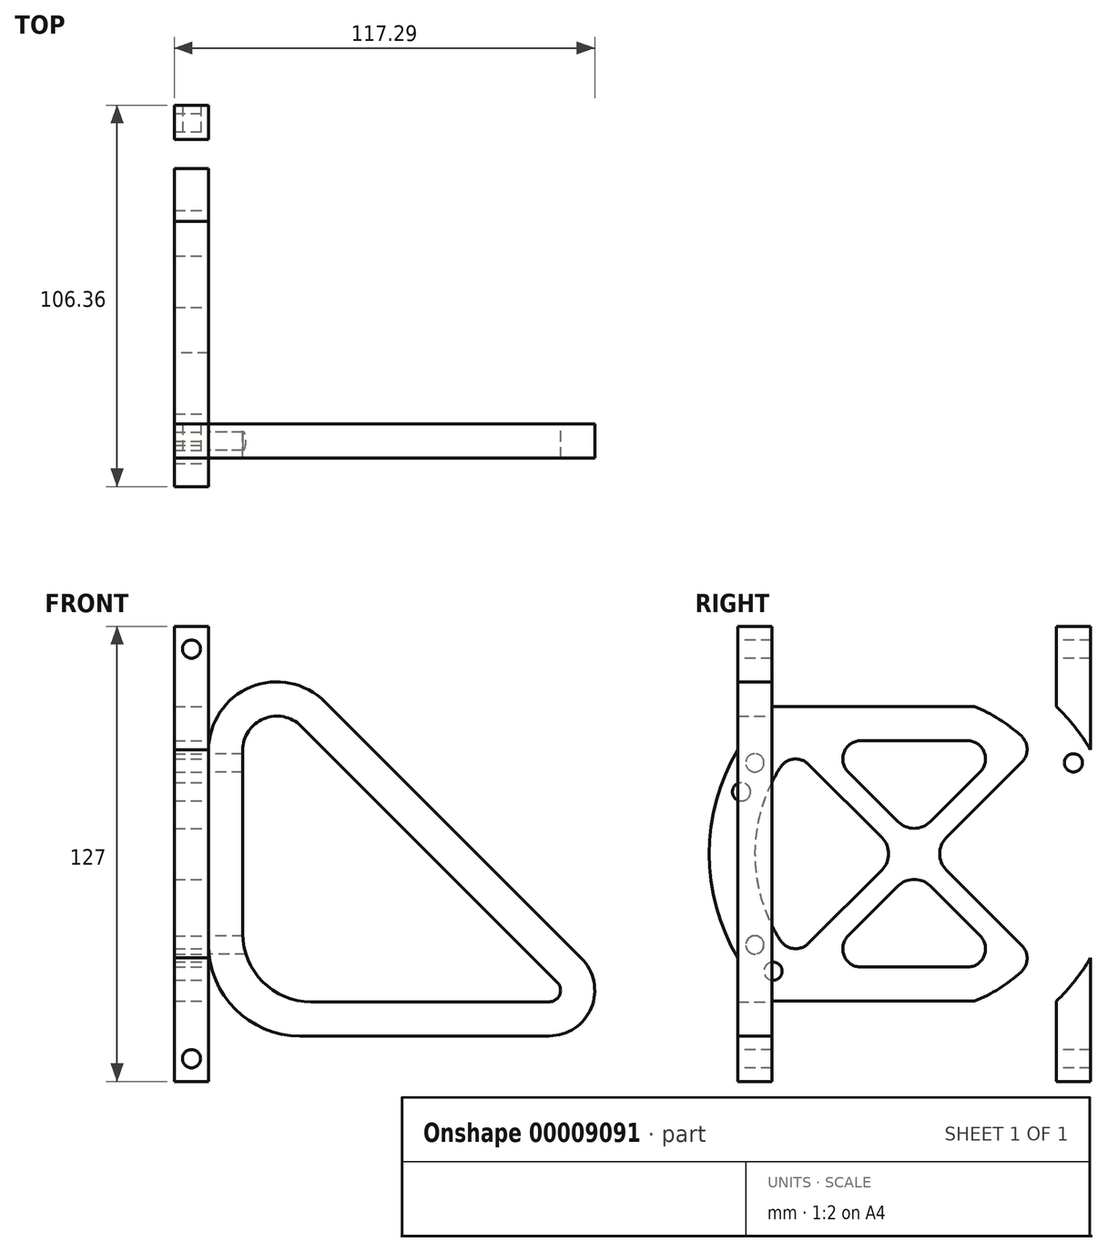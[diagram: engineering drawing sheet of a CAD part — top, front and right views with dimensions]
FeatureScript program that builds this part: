
annotation { "Feature Type Name" : "Feature", "Feature Type Description" : "" }
export const myFeature = defineFeature(function(context is Context, id is Id, definition is map)
    precondition{}
    {
        {
            var Q0;
            Q0=qCreatedBy(makeId("Front.planeOp"),FACE);
            var sketch = newSketch(context, id + "F6", { "sketchPlane" : qUnion([Q0])});
            skLineSegment(sketch, "E0", {"start": v(32.52, -32.52) * mm, "end": v(104.04, -104.04) * mm});
            skLineSegment(sketch, "E1", {"start": v(95.06, -125.72) * mm, "end": v(25.4, -125.72) * mm});
            skLineSegment(sketch, "E2", {"start": v(0, -46) * mm, "end": v(0, -100.32) * mm});
            skLineSegment(sketch, "E3.0", {"start": v(25.79, -39.26) * mm, "end": v(97.3, -110.78) * mm});
            skLineSegment(sketch, "E3.1", {"start": v(9.53, -46) * mm, "end": v(9.53, -97.15) * mm});
            skLineSegment(sketch, "E3.2", {"start": v(95.06, -116.2) * mm, "end": v(28.58, -116.2) * mm});
            skPoint(sketch, "E4.visualSharp", {"position": v(102.73, -116.2) * mm});
            skArc(sketch, "E4.filletArc", {"start": v(95.06, -116.2) * mm, "mid": v(98, -114.24) * mm, "end": v(97.3, -110.78) * mm});
            skPoint(sketch, "E5.visualSharp", {"position": v(9.53, -23) * mm});
            skArc(sketch, "E5.filletArc", {"start": v(25.79, -39.26) * mm, "mid": v(15.4, -37.2) * mm, "end": v(9.53, -46) * mm});
            skPoint(sketch, "E6.visualSharp", {"position": v(9.53, -116.2) * mm});
            skArc(sketch, "E6.filletArc", {"start": v(9.53, -97.15) * mm, "mid": v(15.1, -110.62) * mm, "end": v(28.58, -116.2) * mm});
            skPoint(sketch, "E7.visualSharp", {"position": v(0, -125.72) * mm});
            skArc(sketch, "E7.filletArc", {"start": v(0, -100.32) * mm, "mid": v(7.44, -118.28) * mm, "end": v(25.4, -125.72) * mm});
            skPoint(sketch, "E8.visualSharp", {"position": v(0, 0) * mm});
            skArc(sketch, "E8.filletArc", {"start": v(32.52, -32.52) * mm, "mid": v(11.76, -28.4) * mm, "end": v(0, -46) * mm});
            skPoint(sketch, "E9.visualSharp", {"position": v(125.72, -125.72) * mm});
            skArc(sketch, "E9.filletArc", {"start": v(95.06, -125.72) * mm, "mid": v(106.8, -117.88) * mm, "end": v(104.04, -104.04) * mm});
            skSolve(sketch);
        }
        {
            var Q0;
            Q0=makeQuery(id+"F6.imprint","IMPRINT",FACE,{"disambiguationData":[TD([[makeQuery(id+"F6.imprint","IMPRINT",EDGE,{"derivedFrom":sQuery(id+"F6.wireOp",EDGE,"E0")}),-1.0]])]});
            extrude(context, id + "F7", {"entities" : qUnion([Q0]), "depth" : 9.52 * mm});
        }
        {
            var Q0;
            Q0=makeQuery(id+"F7.opExtrude","SWEPT_FACE",FACE,{"disambiguationData":[OSD([sQuery(id+"F6.wireOp",EDGE,"E2")])]});
            var sketch = newSketch(context, id + "F0", { "sketchPlane" : qUnion([Q0])});
            skLineSegment(sketch, "E10.0", {"start": v(9.53, -46) * mm, "end": v(9.53, -100.32) * mm});
            skLineSegment(sketch, "E11.0", {"start": v(0, -46) * mm, "end": v(0, -100.32) * mm});
            skLineSegment(sketch, "E12.0", {"start": v(9.53, -100.32) * mm, "end": v(9.53, -125.72) * mm});
            skLineSegment(sketch, "E13.0", {"start": v(9.53, -100.32) * mm, "end": v(0, -100.32) * mm});
            skLineSegment(sketch, "E14.0.0", {"start": v(0, -100.32) * mm, "end": v(0, -125.72) * mm});
            skLineSegment(sketch, "E14.0.1", {"start": v(0, -125.72) * mm, "end": v(9.53, -125.72) * mm});
            skLineSegment(sketch, "E14.0.2", {"start": v(9.53, -125.72) * mm, "end": v(9.53, -100.32) * mm});
            skPoint(sketch, "E15.0", {"position": v(0, -125.72) * mm});
            skLineSegment(sketch, "E16.0", {"start": v(9.53, -125.72) * mm, "end": v(0, -125.72) * mm});
            skLineSegment(sketch, "E17.0.0", {"start": v(0, -26.94) * mm, "end": v(0, -46) * mm});
            skLineSegment(sketch, "E17.0.1", {"start": v(0, -46) * mm, "end": v(9.53, -46) * mm});
            skLineSegment(sketch, "E17.0.2", {"start": v(9.53, -46) * mm, "end": v(9.53, -26.94) * mm});
            skLineSegment(sketch, "E17.0.3", {"start": v(9.53, -32.52) * mm, "end": v(0, -32.52) * mm});
            skPoint(sketch, "E18", {"position": v(4.76, -125.72) * mm});
            skCircle(sketch, "E19", {"center": v(4.76, -100.32) * mm, "radius": 2.54 * mm});
            skCircle(sketch, "E20", {"center": v(4.76, -49.52) * mm, "radius": 2.54 * mm});
            skSolve(sketch);
        }
        {
            var Q0;
            Q0=makeQuery(id+"F0.imprint","IMPRINT",FACE,{"disambiguationData":[TD([[makeQuery(id+"F0.imprint","IMPRINT",EDGE,{"derivedFrom":sQuery(id+"F0.wireOp",EDGE,"E19")}),1.0]])]});
            var Q1;
            Q1=makeQuery(id+"F0.imprint","IMPRINT",FACE,{"disambiguationData":[TD([[makeQuery(id+"F0.imprint","IMPRINT",EDGE,{"derivedFrom":sQuery(id+"F0.wireOp",EDGE,"E20")}),1.0]])]});
            extrude(context, id + "F1", {"entities" : qUnion([Q0, Q1]), "operationType" : NewBodyOperationType.REMOVE, "oppositeDirection" : true, "depth" : 12.7 * mm});
        }
        {
            var Q0;
            Q0=makeQuery(id+"F7.opExtrude","SWEPT_FACE",FACE,{"disambiguationData":[OSD([sQuery(id+"F6.wireOp",EDGE,"E0")])]});
            var sketch = newSketch(context, id + "F8", { "sketchPlane" : qUnion([Q0])});
            skLineSegment(sketch, "E21.0", {"start": v(46, 0) * mm, "end": v(147.14, 0) * mm});
            skLineSegment(sketch, "E22.0.0", {"start": v(147.14, -9.53) * mm, "end": v(46, -9.53) * mm});
            skLineSegment(sketch, "E22.0.1", {"start": v(46, -9.53) * mm, "end": v(26.94, -9.53) * mm});
            skLineSegment(sketch, "E22.0.2", {"start": v(32.52, -9.53) * mm, "end": v(70.94, -9.53) * mm});
            skLineSegment(sketch, "E22.0.3", {"start": v(106.86, -9.53) * mm, "end": v(70.94, -9.53) * mm});
            skLineSegment(sketch, "E22.0.4", {"start": v(106.86, -9.53) * mm, "end": v(156.12, -9.53) * mm});
            skLineSegment(sketch, "E22.0.5", {"start": v(159.84, -9.53) * mm, "end": v(147.14, -9.53) * mm});
            skLineSegment(sketch, "E23.0", {"start": v(46, -9.53) * mm, "end": v(147.14, -9.53) * mm});
            skLineSegment(sketch, "E24.0.1", {"start": v(147.14, 0) * mm, "end": v(159.84, 0) * mm});
            skLineSegment(sketch, "E24.0.2", {"start": v(156.12, 0) * mm, "end": v(106.86, 0) * mm});
            skLineSegment(sketch, "E24.0.3", {"start": v(70.94, 0) * mm, "end": v(106.86, 0) * mm});
            skLineSegment(sketch, "E24.0.4", {"start": v(70.94, 0) * mm, "end": v(32.52, 0) * mm});
            skLineSegment(sketch, "E24.0.5", {"start": v(26.94, 0) * mm, "end": v(46, 0) * mm});
            skPoint(sketch, "E25", {"position": v(96.57, 0) * mm});
            skLineSegment(sketch, "E26", {"start": v(96.57, 0) * mm, "end": v(96.57, -9.52) * mm, "construction": true});
            skPoint(sketch, "E27", {"position": v(96.57, -4.76) * mm});
            skCircle(sketch, "E28", {"center": v(128.54, -4.76) * mm, "radius": 2.54 * mm});
            skCircle(sketch, "E29", {"center": v(52.34, -4.76) * mm, "radius": 2.54 * mm});
            skSolve(sketch);
        }
        {
            var Q0;
            Q0=makeQuery(id+"F8.imprint","IMPRINT",FACE,{"disambiguationData":[TD([[makeQuery(id+"F8.imprint","IMPRINT",EDGE,{"derivedFrom":sQuery(id+"F8.wireOp",EDGE,"E29")}),1.0]])]});
            var Q1;
            Q1=makeQuery(id+"F8.imprint","IMPRINT",FACE,{"disambiguationData":[TD([[makeQuery(id+"F8.imprint","IMPRINT",EDGE,{"derivedFrom":sQuery(id+"F8.wireOp",EDGE,"E28")}),1.0]])]});
            extrude(context, id + "F2", {"entities" : qUnion([Q0, Q1]), "operationType" : NewBodyOperationType.REMOVE, "oppositeDirection" : true, "depth" : 12.7 * mm});
        }
        {
            var Q0;
            Q0=makeQuery(id+"F7.opExtrude","SWEPT_FACE",FACE,{"disambiguationData":[OSD([sQuery(id+"F6.wireOp",EDGE,"E2")])]});
            var sketch = newSketch(context, id + "F3", { "sketchPlane" : qUnion([Q0])});
            skCircle(sketch, "E30.0", {"center": v(4.76, -49.52) * mm, "radius": 2.54 * mm});
            skCircle(sketch, "E31.0", {"center": v(4.76, -100.32) * mm, "radius": 2.54 * mm});
            skCircle(sketch, "E32", {"center": v(-39.69, -74.92) * mm, "radius": 51.2 * mm, "construction": true});
            skLineSegment(sketch, "E33", {"start": v(-39.69, -74.92) * mm, "end": v(-39.69, -23.73) * mm, "construction": true});
            skCircle(sketch, "E34.0.MirrorC", {"center": v(-84.14, -49.52) * mm, "radius": 2.54 * mm});
            skCircle(sketch, "E35.0.MirrorC", {"center": v(-84.14, -100.32) * mm, "radius": 2.54 * mm});
            skLineSegment(sketch, "E36", {"start": v(-39.69, -74.92) * mm, "end": v(4.76, -49.52) * mm, "construction": true});
            skLineSegment(sketch, "E37", {"start": v(8.5, -57.63) * mm, "end": v(-39.69, -74.92) * mm, "construction": true});
            skCircle(sketch, "E38", {"center": v(8.5, -57.63) * mm, "radius": 2.54 * mm});
            skCircle(sketch, "E39", {"center": v(-79.05, -42.2) * mm, "radius": 2.54 * mm});
            skCircle(sketch, "E40", {"center": v(-87.87, -92.22) * mm, "radius": 2.54 * mm});
            skCircle(sketch, "E41", {"center": v(-0.32, -107.66) * mm, "radius": 2.54 * mm});
            skArc(sketch, "E42", {"start": v(-79.38, -33.8) * mm, "mid": v(-96.84, -74.92) * mm, "end": v(-79.38, -116.05) * mm});
            skArc(sketch, "E43.0", {"start": v(-56.56, -33.8) * mm, "mid": v(-84.14, -74.92) * mm, "end": v(-56.56, -116.05) * mm});
            skLineSegment(sketch, "E44", {"start": v(9.52, -103.98) * mm, "end": v(9.53, -138.42) * mm});
            skLineSegment(sketch, "E45", {"start": v(9.53, -138.42) * mm, "end": v(0, -138.42) * mm});
            skLineSegment(sketch, "E46", {"start": v(0, -138.42) * mm, "end": v(0, -116.05) * mm});
            skLineSegment(sketch, "E47.0", {"start": v(9.53, -46) * mm, "end": v(9.53, -100.32) * mm, "construction": true});
            skLineSegment(sketch, "E48", {"start": v(9.53, -45.87) * mm, "end": v(9.53, -11.42) * mm});
            skLineSegment(sketch, "E49", {"start": v(9.53, -11.42) * mm, "end": v(0, -11.42) * mm});
            skLineSegment(sketch, "E50", {"start": v(0, -11.42) * mm, "end": v(0, -33.8) * mm});
            skLineSegment(sketch, "E51.0.MirrorCS", {"start": v(-88.9, -45.87) * mm, "end": v(-88.9, -11.42) * mm});
            skLineSegment(sketch, "E52.0.MirrorCS", {"start": v(-88.9, -11.42) * mm, "end": v(-79.38, -11.42) * mm});
            skLineSegment(sketch, "E53.0.MirrorCS", {"start": v(-79.38, -11.42) * mm, "end": v(-79.38, -33.8) * mm});
            skLineSegment(sketch, "E54.0.MirrorCS", {"start": v(-88.9, -103.98) * mm, "end": v(-88.9, -138.42) * mm});
            skLineSegment(sketch, "E55.0.MirrorCS", {"start": v(-88.9, -138.42) * mm, "end": v(-79.38, -138.42) * mm});
            skLineSegment(sketch, "E56.0.MirrorCS", {"start": v(-79.38, -138.42) * mm, "end": v(-79.38, -116.05) * mm});
            skLineSegment(sketch, "E57", {"start": v(-10.58, -41.33) * mm, "end": v(-35.2, -65.94) * mm});
            skLineSegment(sketch, "E58", {"start": v(-44.18, -65.94) * mm, "end": v(-68.8, -41.33) * mm});
            skLineSegment(sketch, "E59", {"start": v(-73.28, -45.82) * mm, "end": v(-48.67, -70.43) * mm});
            skLineSegment(sketch, "E60", {"start": v(-48.67, -79.41) * mm, "end": v(-73.28, -104.03) * mm});
            skLineSegment(sketch, "E61", {"start": v(-68.8, -108.52) * mm, "end": v(-44.18, -83.9) * mm});
            skLineSegment(sketch, "E62", {"start": v(-35.2, -83.9) * mm, "end": v(-10.58, -108.52) * mm});
            skLineSegment(sketch, "E63", {"start": v(-6.1, -45.82) * mm, "end": v(-30.7, -70.43) * mm});
            skLineSegment(sketch, "E64", {"start": v(-30.7, -79.41) * mm, "end": v(-6.1, -104.03) * mm});
            skPoint(sketch, "E65.visualSharp", {"position": v(-44.18, -74.92) * mm});
            skArc(sketch, "E65.filletArc", {"start": v(-48.67, -79.41) * mm, "mid": v(-46.8, -74.92) * mm, "end": v(-48.67, -70.43) * mm});
            skPoint(sketch, "E66.visualSharp", {"position": v(-39.69, -70.43) * mm});
            skArc(sketch, "E66.filletArc", {"start": v(-44.18, -65.94) * mm, "mid": v(-39.69, -67.8) * mm, "end": v(-35.2, -65.94) * mm});
            skPoint(sketch, "E67.visualSharp", {"position": v(-35.2, -74.92) * mm});
            skArc(sketch, "E67.filletArc", {"start": v(-30.7, -70.43) * mm, "mid": v(-32.57, -74.92) * mm, "end": v(-30.7, -79.41) * mm});
            skPoint(sketch, "E68.visualSharp", {"position": v(-39.69, -79.41) * mm});
            skArc(sketch, "E68.filletArc", {"start": v(-35.2, -83.9) * mm, "mid": v(-39.69, -82.04) * mm, "end": v(-44.18, -83.9) * mm});
            skLineSegment(sketch, "E69", {"start": v(-79.38, -33.8) * mm, "end": v(0, -33.8) * mm});
            skLineSegment(sketch, "E70", {"start": v(-79.38, -116.05) * mm, "end": v(0, -116.05) * mm});
            skArc(sketch, "E71.trimOffspring", {"start": v(0, -116.05) * mm, "mid": v(17.46, -74.92) * mm, "end": v(0, -33.8) * mm});
            skArc(sketch, "E72.trimOffspring", {"start": v(-22.81, -116.05) * mm, "mid": v(3.92, -66.32) * mm, "end": v(-39.69, -30.47) * mm});
            skLineSegment(sketch, "E73", {"start": v(-66.8, -106.52) * mm, "end": v(-12.58, -106.52) * mm});
            skLineSegment(sketch, "E74", {"start": v(-66.8, -43.33) * mm, "end": v(-12.58, -43.33) * mm});
            skSolve(sketch);
        }
        {
            var Q0;
            Q0=makeQuery(id+"F3.imprint","IMPRINT",FACE,{"disambiguationData":[TD([[makeQuery(id+"F3.imprint","IMPRINT",EDGE,{"derivedFrom":sQuery(id+"F3.wireOp",EDGE,"E34.0.MirrorC")}),1.0]])]});
            var Q1;
            Q1=makeQuery(id+"F3.imprint","IMPRINT",FACE,{"disambiguationData":[TD([[makeQuery(id+"F3.imprint","IMPRINT",EDGE,{"derivedFrom":sQuery(id+"F3.wireOp",EDGE,"E30.0")}),-1.0]])]});
            var Q2;
            {var subQ0=makeQuery(id+"F7.opExtrude","CAP_EDGE",EDGE,{"disambiguationData":[OSD([sQuery(id+"F6.wireOp",EDGE,"E2")])],"isStart":false});var subQ1=sQuery(id+"F3.wireOp",EDGE,"E38");var subQ5=makeQuery(id+"F3.imprint","INTERSECT",VERTEX,{"disambiguationData":[OD(0.0)],"derivedFrom":[subQ0,subQ1]});Q2=makeQuery(id+"F3.imprint","IMPRINT",FACE,{"disambiguationData":[TD([[makeQuery(id+"F3.imprint","IMPRINT",EDGE,{"disambiguationData":[TD([[subQ5,1.0]])],"derivedFrom":subQ1}),-1.0]])]});}
            var Q3;
            {var subQ1=sQuery(id+"F3.wireOp",EDGE,"E54.0.MirrorCS");Q3=makeQuery(id+"F3.imprint","IMPRINT",FACE,{"disambiguationData":[TD([[makeQuery(id+"F3.imprint","IMPRINT",EDGE,{"derivedFrom":subQ1}),1.0]])]});}
            var Q4;
            {var subQ1=sQuery(id+"F3.wireOp",EDGE,"E51.0.MirrorCS");Q4=makeQuery(id+"F3.imprint","IMPRINT",FACE,{"disambiguationData":[TD([[makeQuery(id+"F3.imprint","IMPRINT",EDGE,{"derivedFrom":subQ1}),-1.0]])]});}
            var Q5;
            {var subQ2=sQuery(id+"F3.wireOp",EDGE,"E49");Q5=makeQuery(id+"F3.imprint","IMPRINT",FACE,{"disambiguationData":[TD([[makeQuery(id+"F3.imprint","IMPRINT",EDGE,{"derivedFrom":subQ2}),1.0]])]});}
            var Q6;
            {var subQ2=sQuery(id+"F3.wireOp",EDGE,"E45");Q6=makeQuery(id+"F3.imprint","IMPRINT",FACE,{"disambiguationData":[TD([[makeQuery(id+"F3.imprint","IMPRINT",EDGE,{"derivedFrom":subQ2}),-1.0]])]});}
            var Q7;
            {var subQ0=sQuery(id+"F6.wireOp",EDGE,"E2");var subQ1=makeQuery(id+"F7.opExtrude","SWEPT_EDGE",EDGE,{"disambiguationData":[OSD([subQ0,sQuery(id+"F6.wireOp",EDGE,"E7.filletArc")])]});Q7=makeQuery(id+"F3.imprint","IMPRINT",FACE,{"disambiguationData":[TD([[makeQuery(id+"F3.imprint","IMPRINT",EDGE,{"derivedFrom":subQ1}),-1.0]])]});}
            var Q8;
            {var subQ16=sQuery(id+"F3.wireOp",EDGE,"E59");Q8=makeQuery(id+"F3.imprint","IMPRINT",FACE,{"disambiguationData":[TD([[makeQuery(id+"F3.imprint","IMPRINT",EDGE,{"derivedFrom":subQ16}),1.0]])]});}
            var Q9;
            {var subQ0=sQuery(id+"F3.wireOp",EDGE,"E74");Q9=makeQuery(id+"F3.imprint","IMPRINT",FACE,{"disambiguationData":[TD([[makeQuery(id+"F3.imprint","IMPRINT",EDGE,{"derivedFrom":subQ0}),1.0]])]});}
            var Q10;
            {var subQ1=sQuery(id+"F3.wireOp",EDGE,"E72.trimOffspring");var subQ7=makeQuery(id+"F3.imprint","INTERSECT",VERTEX,{"derivedFrom":[sQuery(id+"F3.wireOp",EDGE,"E63"),subQ1]});Q10=makeQuery(id+"F3.imprint","IMPRINT",FACE,{"disambiguationData":[TD([[makeQuery(id+"F3.imprint","IMPRINT",EDGE,{"disambiguationData":[TD([[subQ7,1.0]])],"derivedFrom":subQ1}),-1.0]])]});}
            var Q11;
            Q11=makeQuery(id+"F3.imprint","IMPRINT",FACE,{"disambiguationData":[TD([[makeQuery(id+"F3.imprint","IMPRINT",EDGE,{"derivedFrom":sQuery(id+"F3.wireOp",EDGE,"E41")}),-1.0]])]});
            var Q12;
            {var subQ0=sQuery(id+"F3.wireOp",EDGE,"E73");Q12=makeQuery(id+"F3.imprint","IMPRINT",FACE,{"disambiguationData":[TD([[makeQuery(id+"F3.imprint","IMPRINT",EDGE,{"derivedFrom":subQ0}),-1.0]])]});}
            var Q13;
            {var subQ0=sQuery(id+"F6.wireOp",EDGE,"E2");var subQ1=makeQuery(id+"F7.opExtrude","SWEPT_EDGE",EDGE,{"disambiguationData":[OSD([subQ0,sQuery(id+"F6.wireOp",EDGE,"E8.filletArc")])]});Q13=makeQuery(id+"F3.imprint","IMPRINT",FACE,{"disambiguationData":[TD([[makeQuery(id+"F3.imprint","IMPRINT",EDGE,{"derivedFrom":subQ1}),1.0]])]});}
            extrude(context, id + "F9", {"entities" : qUnion([Q0, Q1, Q2, Q3, Q4, Q5, Q6, Q7, Q8, Q9, Q10, Q11, Q12, Q13]), "depth" : 9.52 * mm});
        }
        {
            var Q0;
            Q0=makeQuery(id+"F9.opExtrude","SWEPT_EDGE",EDGE,{"disambiguationData":[OSD([sQuery(id+"F3.wireOp",EDGE,"E43.0"),sQuery(id+"F3.wireOp",EDGE,"E59")])]});
            var Q1;
            Q1=makeQuery(id+"F9.opExtrude","SWEPT_EDGE",EDGE,{"disambiguationData":[OSD([sQuery(id+"F3.wireOp",EDGE,"E43.0"),sQuery(id+"F3.wireOp",EDGE,"E60")])]});
            var Q2;
            Q2=makeQuery(id+"F9.opExtrude","SWEPT_EDGE",EDGE,{"disambiguationData":[OSD([sQuery(id+"F3.wireOp",EDGE,"E58"),sQuery(id+"F3.wireOp",EDGE,"E74")])]});
            var Q3;
            Q3=makeQuery(id+"F9.opExtrude","SWEPT_EDGE",EDGE,{"disambiguationData":[OSD([sQuery(id+"F3.wireOp",EDGE,"E61"),sQuery(id+"F3.wireOp",EDGE,"E73")])]});
            var Q4;
            Q4=makeQuery(id+"F9.opExtrude","SWEPT_EDGE",EDGE,{"disambiguationData":[OSD([sQuery(id+"F3.wireOp",EDGE,"E62"),sQuery(id+"F3.wireOp",EDGE,"E73")])]});
            var Q5;
            Q5=makeQuery(id+"F9.opExtrude","SWEPT_EDGE",EDGE,{"disambiguationData":[OSD([sQuery(id+"F3.wireOp",EDGE,"E57"),sQuery(id+"F3.wireOp",EDGE,"E74")])]});
            var Q6;
            Q6=makeQuery(id+"F9.opExtrude","SWEPT_EDGE",EDGE,{"disambiguationData":[OSD([sQuery(id+"F3.wireOp",EDGE,"E63"),sQuery(id+"F3.wireOp",EDGE,"E72.trimOffspring")])]});
            var Q7;
            Q7=makeQuery(id+"F9.opExtrude","SWEPT_EDGE",EDGE,{"disambiguationData":[OSD([sQuery(id+"F3.wireOp",EDGE,"E64"),sQuery(id+"F3.wireOp",EDGE,"E72.trimOffspring")])]});
            fillet(context, id + "F10", {"entities" : qUnion([Q0, Q1, Q2, Q3, Q4, Q5, Q6, Q7]), "radius" : 5.08 * mm, "tangentPropagation" : true, "allowEdgeOverflow" : false});
        }
        {
            var Q0;
            Q0=makeQuery(id+"F9.opExtrude","SWEPT_FACE",FACE,{"disambiguationData":[OSD([sQuery(id+"F3.wireOp",EDGE,"E48")])]});
            var sketch = newSketch(context, id + "F4", { "sketchPlane" : qUnion([Q0])});
            skLineSegment(sketch, "E75.0.0", {"start": v(0, -45.87) * mm, "end": v(0, -11.42) * mm});
            skLineSegment(sketch, "E75.0.1", {"start": v(0, -11.42) * mm, "end": v(-9.53, -11.42) * mm});
            skLineSegment(sketch, "E75.0.2", {"start": v(-9.53, -11.42) * mm, "end": v(-9.53, -45.87) * mm});
            skLineSegment(sketch, "E75.0.3", {"start": v(-9.53, -45.87) * mm, "end": v(0, -45.87) * mm});
            skLineSegment(sketch, "E76.0.0", {"start": v(0, -138.42) * mm, "end": v(0, -103.98) * mm});
            skLineSegment(sketch, "E76.0.1", {"start": v(0, -103.98) * mm, "end": v(-9.53, -103.98) * mm});
            skLineSegment(sketch, "E76.0.2", {"start": v(-9.53, -103.98) * mm, "end": v(-9.53, -138.42) * mm});
            skLineSegment(sketch, "E76.0.3", {"start": v(-9.53, -138.42) * mm, "end": v(0, -138.42) * mm});
            skLineSegment(sketch, "E77.0.0", {"start": v(0, -103.98) * mm, "end": v(0, -45.87) * mm});
            skLineSegment(sketch, "E77.0.1", {"start": v(0, -45.87) * mm, "end": v(-9.53, -45.87) * mm});
            skLineSegment(sketch, "E77.0.2", {"start": v(-9.53, -45.87) * mm, "end": v(-9.53, -103.98) * mm});
            skLineSegment(sketch, "E77.0.3", {"start": v(-9.53, -103.98) * mm, "end": v(0, -103.98) * mm});
            skCircle(sketch, "E78", {"center": v(-4.76, -17.77) * mm, "radius": 2.54 * mm});
            skCircle(sketch, "E79", {"center": v(-4.76, -132.07) * mm, "radius": 2.54 * mm});
            skPoint(sketch, "E80", {"position": v(-4.76, -11.42) * mm});
            skLineSegment(sketch, "E81", {"start": v(0, -74.92) * mm, "end": v(-9.53, -74.92) * mm});
            skSolve(sketch);
        }
        {
            var Q0;
            Q0=makeQuery(id+"F4.imprint","IMPRINT",FACE,{"disambiguationData":[TD([[makeQuery(id+"F4.imprint","IMPRINT",EDGE,{"derivedFrom":sQuery(id+"F4.wireOp",EDGE,"E78")}),1.0]])]});
            var Q1;
            Q1=makeQuery(id+"F4.imprint","IMPRINT",FACE,{"disambiguationData":[TD([[makeQuery(id+"F4.imprint","IMPRINT",EDGE,{"derivedFrom":sQuery(id+"F4.wireOp",EDGE,"E79")}),1.0]])]});
            extrude(context, id + "F5", {"entities" : qUnion([Q0, Q1]), "operationType" : NewBodyOperationType.REMOVE, "endBound" : BoundingType.THROUGH_ALL, "oppositeDirection" : true, "depth" : 25.4 * mm});
        }
    });
